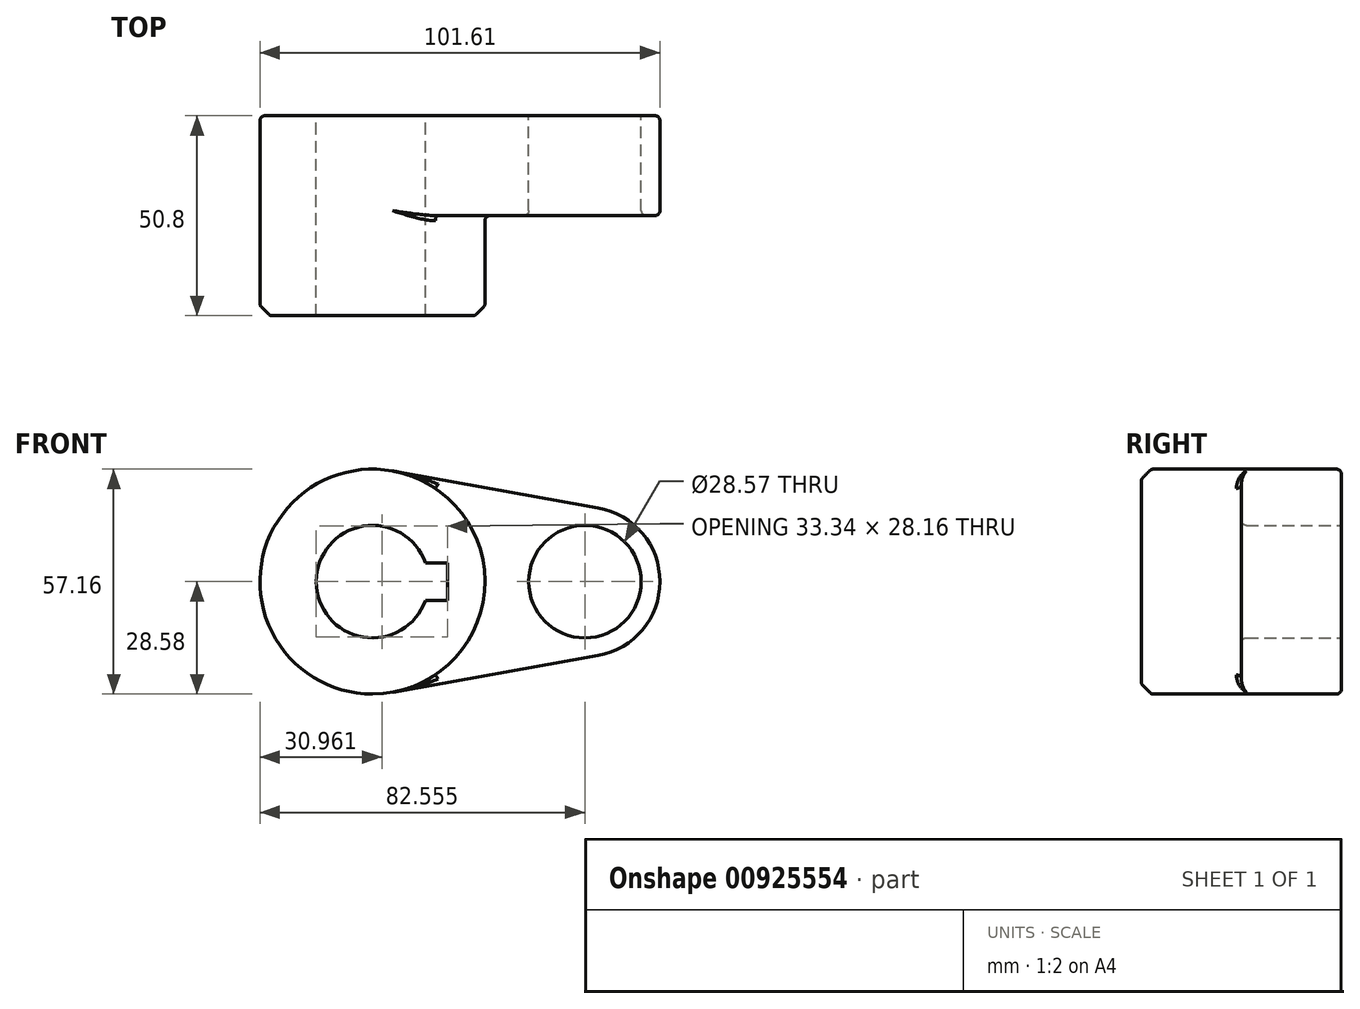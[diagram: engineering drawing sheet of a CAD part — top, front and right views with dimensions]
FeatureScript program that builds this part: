
annotation { "Feature Type Name" : "Feature", "Feature Type Description" : "" }
export const myFeature = defineFeature(function(context is Context, id is Id, definition is map)
    precondition{}
    {
        {
            var Q0;
            Q0=qCreatedBy(makeId("Front.planeOp"),FACE);
            var sketch = newSketch(context, id + "F0", { "sketchPlane" : qUnion([Q0])});
            skCircle(sketch, "E0", {"center": v(0, 0) * mm, "radius": 28.58 * mm});
            skCircle(sketch, "E1", {"center": v(53.98, 0) * mm, "radius": 19.05 * mm});
            skLineSegment(sketch, "E2", {"start": v(5.04, 28.13) * mm, "end": v(57.34, 18.75) * mm});
            skLineSegment(sketch, "E3", {"start": v(5.04, -28.13) * mm, "end": v(57.34, -18.75) * mm});
            skCircle(sketch, "E4", {"center": v(0, 0) * mm, "radius": 14.29 * mm});
            skCircle(sketch, "E5", {"center": v(53.98, 0) * mm, "radius": 14.29 * mm});
            skLineSegment(sketch, "E6.bottom", {"start": v(-19.05, 4.76) * mm, "end": v(19.05, 4.76) * mm});
            skLineSegment(sketch, "E6.top", {"start": v(-19.05, -4.76) * mm, "end": v(19.05, -4.76) * mm});
            skLineSegment(sketch, "E6.left", {"start": v(-19.05, 4.76) * mm, "end": v(-19.05, -4.76) * mm});
            skLineSegment(sketch, "E6.right", {"start": v(19.05, 4.76) * mm, "end": v(19.05, -4.76) * mm});
            skSolve(sketch);
        }
        {
            var Q0;
            {var subQ7=sQuery(id+"F0.wireOp",EDGE,"E6.left");Q0=makeQuery(id+"F0.imprint","IMPRINT",FACE,{"disambiguationData":[TD([[makeQuery(id+"F0.imprint","IMPRINT",EDGE,{"derivedFrom":subQ7}),-1.0]])]});}
            var Q1;
            Q1=makeQuery(id+"F0.imprint","IMPRINT",FACE,{"disambiguationData":[TD([[makeQuery(id+"F0.imprint","IMPRINT",EDGE,{"derivedFrom":sQuery(id+"F0.wireOp",EDGE,"E5")}),-1.0]])]});
            var Q2;
            {var subQ0=sQuery(id+"F0.wireOp",EDGE,"E2");Q2=makeQuery(id+"F0.imprint","IMPRINT",FACE,{"disambiguationData":[TD([[makeQuery(id+"F0.imprint","IMPRINT",EDGE,{"derivedFrom":subQ0}),-1.0]])]});}
            var Q3;
            {var subQ5=sQuery(id+"F0.wireOp",EDGE,"E6.left");Q3=makeQuery(id+"F0.imprint","IMPRINT",FACE,{"disambiguationData":[TD([[makeQuery(id+"F0.imprint","IMPRINT",EDGE,{"derivedFrom":subQ5}),1.0]])]});}
            extrude(context, id + "F1", {"entities" : qUnion([Q0, Q1, Q2, Q3]), "depth" : 25.4 * mm, "offsetDistance" : 25.4 * mm});
        }
        {
            var Q0;
            {var subQ7=sQuery(id+"F0.wireOp",EDGE,"E6.left");Q0=makeQuery(id+"F0.imprint","IMPRINT",FACE,{"disambiguationData":[TD([[makeQuery(id+"F0.imprint","IMPRINT",EDGE,{"derivedFrom":subQ7}),-1.0]])]});}
            var Q1;
            {var subQ5=sQuery(id+"F0.wireOp",EDGE,"E6.left");Q1=makeQuery(id+"F0.imprint","IMPRINT",FACE,{"disambiguationData":[TD([[makeQuery(id+"F0.imprint","IMPRINT",EDGE,{"derivedFrom":subQ5}),1.0]])]});}
            extrude(context, id + "F2", {"entities" : qUnion([Q0, Q1]), "operationType" : NewBodyOperationType.ADD, "depth" : 50.8 * mm, "offsetDistance" : 25.4 * mm});
        }
        {
            var Q0;
            Q0=makeQuery(id+"F2.opExtrude","CAP_EDGE",EDGE,{"disambiguationData":[OSD([sQuery(id+"F0.wireOp",EDGE,"E0")])],"isStart":false});
            chamfer(context, id + "F3", {"entities" : qUnion([Q0]), "width" : 2.54 * mm, "tangentPropagation" : true});
        }
        {
            var Q0;
            {var subQ0=sQuery(id+"F0.wireOp",EDGE,"E0");Q0=makeQuery(id+"F3.opChamfer","BLEND_EDGE",EDGE,{"blendedFrom":[makeQuery(id+"F2.opExtrude","CAP_EDGE",EDGE,{"disambiguationData":[OSD([subQ0])],"isStart":false}),makeQuery(id+"F2.opExtrude","CAP_FACE",FACE,{"disambiguationData":[OSD([subQ0,sQuery(id+"F0.wireOp",EDGE,"E4"),sQuery(id+"F0.wireOp",EDGE,"E6.bottom"),sQuery(id+"F0.wireOp",EDGE,"E6.top"),sQuery(id+"F0.wireOp",EDGE,"E6.right")])],"isStart":false})],"blendedInto":[makeQuery(id+"F2.opExtrude","CAP_FACE",FACE,{"disambiguationData":[OSD([subQ0,sQuery(id+"F0.wireOp",EDGE,"E4"),sQuery(id+"F0.wireOp",EDGE,"E6.bottom"),sQuery(id+"F0.wireOp",EDGE,"E6.top"),sQuery(id+"F0.wireOp",EDGE,"E6.right")])],"isStart":false})]});}
            var Q1;
            {var subQ0=sQuery(id+"F0.wireOp",EDGE,"E0");Q1=makeQuery(id+"F3.opChamfer","BLEND_EDGE",EDGE,{"blendedFrom":[makeQuery(id+"F2.opExtrude","CAP_EDGE",EDGE,{"disambiguationData":[OSD([subQ0])],"isStart":false}),makeQuery(id+"F2.boolean.opBoolean","MERGE",FACE,{"derivedFrom":[makeQuery(id+"F1.opExtrude","SWEPT_FACE",FACE,{"disambiguationData":[OSD([subQ0])]}),makeQuery(id+"F2.opExtrude","SWEPT_FACE",FACE,{"disambiguationData":[OSD([subQ0])]})]})],"blendedInto":[makeQuery(id+"F2.boolean.opBoolean","MERGE",FACE,{"derivedFrom":[makeQuery(id+"F1.opExtrude","SWEPT_FACE",FACE,{"disambiguationData":[OSD([subQ0])]}),makeQuery(id+"F2.opExtrude","SWEPT_FACE",FACE,{"disambiguationData":[OSD([subQ0])]})]})]});}
            var Q2;
            Q2=makeQuery(id+"F1.opExtrude","CAP_FACE",FACE,{"disambiguationData":[OSD([sQuery(id+"F0.wireOp",EDGE,"E0"),sQuery(id+"F0.wireOp",EDGE,"E1"),sQuery(id+"F0.wireOp",EDGE,"E2"),sQuery(id+"F0.wireOp",EDGE,"E3"),sQuery(id+"F0.wireOp",EDGE,"E4"),sQuery(id+"F0.wireOp",EDGE,"E5"),sQuery(id+"F0.wireOp",EDGE,"E6.bottom"),sQuery(id+"F0.wireOp",EDGE,"E6.top"),sQuery(id+"F0.wireOp",EDGE,"E6.right")])],"isStart":false});
            var Q3;
            Q3=makeQuery(id+"F1.opExtrude","CAP_EDGE",EDGE,{"disambiguationData":[OSD([sQuery(id+"F0.wireOp",EDGE,"E1")])],"isStart":true});
            fillet(context, id + "F4", {"entities" : qUnion([Q0, Q1, Q2, Q3]), "radius" : 1.27 * mm, "tangentPropagation" : true, "allowEdgeOverflow" : false});
        }
    });
